# Revit family: 29961 Трибуна однорядная мобильная на 3 места «Сингл-3» Хоббика
name_source: partatom
category: Антураж
revit_build: Autodesk Revit 2018 (Build: 20180423_1000(x64)
units: mm (PartAtom-declared; Revit-internal decimal feet)

## family parameters
Всегда вертикально = Да
Источник визуального образа = Геометрия семейства
На основе рабочей плоскости = Нет
Общий = Нет
При загрузке вырезать с полостями = Нет
Точка расчета площади = Нет

## types (1)
- Трибуна однорядная мобильная на 3 места «Сингл-3»
    URL = https://hobbyka.ru
    Артикул товара = Арт. 29961
    Высота = 700 мм
    Группа модели = Мобильные и стационарные трибуны
    Длина = 1600 мм
    Изготовитель = ООО «Хоббика»
    Изображение типоразмера = Трибуна однорядная мобильная на 3 места «Сингл-3» Арт 29961.jpg
    Материал изделия = Сталь, пластик
    Описание = Трибуна однорядная мобильная на 3 места «Сингл-3»
    Цвет каркаса = Сталь
    Цвет сидений = Красный
    Ширина = 530 мм

## geometry (parser evidence)
native form markers: Sweep x3
no freeform markers — native parametric forms only
